# Revit family: AVAB_Roof_Exhauster
name_source: partatom
category: Mechanical Equipment
units: mm (PartAtom-declared; Revit-internal decimal feet)

## family parameters
Always vertical = Yes
Cut with Voids When Loaded = No
Part Type = Normal
Room Calculation Point = No
Round Connector Dimension = Use Diameter
Shared = No
Work Plane-Based = No

## types (8) — shared parameters
0 = 0' - 0"
1" = 0' - 1"
1.5 = 0' - 1 1/2"
2" = 0' - 2"
2' = 2' - 0"
3" = 0' - 3"
30 = 30.00°
4" = 0' - 4"
60 = 60.00°
Manufacturer = Loren Cook Company
Model = AVAB
ONE EIGTH = 0' - 0 1/8"
Type Comments = Adjustable Pitch Vane Axial Roof Exhauster Belt Drive Arrangement 9
URL = www.lorencook.com

## per-type parameters (varying)
- 35_AVAB_ROOF_EXHAUSTER: (A+.25")/2=1' - 5 7/8"; (B/2)+2"=1' - 9 15/16"; (E-.25")/2=1' - 9 3/8"; (E/2)-2"=1' - 7 1/2"; (H-(A/2))/2=1' - 3 1/16"; (T_SQ/2)+.125"=1' - 11 1/8"; -(E-.25")/2=-1' - 9 3/8"; -(E/2)+2"=-1' - 7 1/2"; -E/2=-1' - 9 1/2"; A=2' - 11 1/2"; A/2=1' - 5 3/4"; A/3=1' - 2 3/16"; B=3' - 3 7/8"; B/2=1' - 7 15/16"; C=3' - 2"; C/2=1' - 7"; C/2+L=3' - 6"; E=3' - 7"; E-2"=3' - 5"; E/2=1' - 9 1/2"; F=0' - 0 9/16"; F/2=0' - 0 9/32"; G=12' - 0"; H=3' - 11 7/8"; H+L=5' - 10 7/8"; H-(A/2)=2' - 6 1/8"; J=3' - 3 3/4"; J/2=1' - 7 7/8"; K=0' - 1 5/8"; K+K=0' - 3 1/4"; L=1' - 11"; L-(C/2)=0' - 4"; L-.125"=1' - 10 7/8"; M=3' - 5"; M/2=1' - 8 1/2"; N=1' - 0"; P=0' - 0 5/8"; P/2=0' - 0 5/16"; RO=3' - 5 1/2"; RO/2=1' - 8 3/4"; T_SQ=3' - 10"; UP_A=6' - 0"
- 39_AVAB_ROOF_EXHAUSTER: (A+.25")/2=1' - 7 13/16"; (B/2)+2"=1' - 11 31/32"; (E-.25")/2=1' - 9 3/8"; (E/2)-2"=1' - 7 1/2"; (H-(A/2))/2=1' - 3 3/32"; (T_SQ/2)+.125"=2' - 1 1/8"; -(E-.25")/2=-1' - 9 3/8"; -(E/2)+2"=-1' - 7 1/2"; -E/2=-1' - 9 1/2"; A=3' - 3 3/8"; A/2=1' - 7 11/16"; A/3=1' - 3 3/4"; B=3' - 7 15/16"; B/2=1' - 9 31/32"; C=3' - 5 7/8"; C/2=1' - 8 15/16"; C/2+L=3' - 10 15/16"; E=3' - 7"; E-2"=3' - 5"; E/2=1' - 9 1/2"; F=0' - 0 9/16"; F/2=0' - 0 9/32"; G=12' - 0"; H=4' - 1 7/8"; H+L=6' - 3 7/8"; H-(A/2)=2' - 6 3/16"; J=3' - 3 1/2"; J/2=1' - 7 3/4"; K=0' - 1 3/4"; K+K=0' - 3 1/2"; L=2' - 2"; L-(C/2)=0' - 5 1/16"; L-.125"=2' - 1 7/8"; M=3' - 9"; M/2=1' - 10 1/2"; N=1' - 1 3/8"; P=0' - 0 5/8"; P/2=0' - 0 5/16"; RO=3' - 9 1/2"; RO/2=1' - 10 3/4"; T_SQ=4' - 2"; UP_A=6' - 0"
- 44_AVAB_ROOF_EXHAUSTER: (A+.25")/2=1' - 10 3/16"; (B/2)+2"=2' - 2 13/16"; (E-.25")/2=1' - 11 3/8"; (E/2)-2"=1' - 9 1/2"; (H-(A/2))/2=1' - 3 19/32"; (T_SQ/2)+.125"=2' - 3 7/8"; -(E-.25")/2=-1' - 11 3/8"; -(E/2)+2"=-1' - 9 1/2"; -E/2=-1' - 11 1/2"; A=3' - 8 1/8"; A/2=1' - 10 1/16"; A/3=1' - 5 21/32"; B=4' - 1 5/8"; B/2=2' - 0 13/16"; C=3' - 11 3/8"; C/2=1' - 11 11/16"; C/2+L=4' - 4 3/16"; E=3' - 11"; E-2"=3' - 9"; E/2=1' - 11 1/2"; F=0' - 0 9/16"; F/2=0' - 0 9/32"; G=12' - 0"; H=4' - 5 1/4"; H+L=6' - 9 3/4"; H-(A/2)=2' - 7 3/16"; J=3' - 7 1/2"; J/2=1' - 9 3/4"; K=0' - 1 3/4"; K+K=0' - 3 1/2"; L=2' - 4 1/2"; L-(C/2)=0' - 4 13/16"; L-.125"=2' - 4 3/8"; M=4' - 3"; M/2=2' - 1 1/2"; N=1' - 3 3/8"; P=0' - 0 5/8"; P/2=0' - 0 5/16"; RO=4' - 3"; RO/2=2' - 1 1/2"; T_SQ=4' - 7 1/2"; UP_A=6' - 4"
- 49_AVAB_ROOF_EXHAUSTER: (A+.25")/2=2' - 0 3/4"; (B/2)+2"=2' - 5 3/8"; (E-.25")/2=1' - 11 3/8"; (E/2)-2"=1' - 9 1/2"; (H-(A/2))/2=1' - 2 9/16"; (T_SQ/2)+.125"=2' - 6 3/8"; -(E-.25")/2=-1' - 11 3/8"; -(E/2)+2"=-1' - 9 1/2"; -E/2=-1' - 11 1/2"; A=4' - 1 1/4"; A/2=2' - 0 5/8"; A/3=1' - 7 11/16"; B=4' - 6 3/4"; B/2=2' - 3 3/8"; C=4' - 4 1/2"; C/2=2' - 2 1/4"; C/2+L=4' - 9 3/4"; E=3' - 11"; E-2"=3' - 9"; E/2=1' - 11 1/2"; F=0' - 0 9/16"; F/2=0' - 0 9/32"; G=12' - 0"; H=4' - 5 3/4"; H+L=7' - 1 1/4"; H-(A/2)=2' - 5 1/8"; J=3' - 7 1/2"; J/2=1' - 9 3/4"; K=0' - 1 3/4"; K+K=0' - 3 1/2"; L=2' - 7 1/2"; L-(C/2)=0' - 5 1/4"; L-.125"=2' - 7 3/8"; M=4' - 8"; M/2=2' - 4"; N=1' - 5"; P=0' - 0 5/8"; P/2=0' - 0 5/16"; RO=4' - 8"; RO/2=2' - 4"; T_SQ=5' - 0 1/2"; UP_A=7' - 4 1/2"
- 57_AVAB_ROOF_EXHAUSTER: (A+.25")/2=2' - 4 11/16"; (B/2)+2"=2' - 9 5/16"; (E-.25")/2=2' - 6 3/8"; (E/2)-2"=2' - 4 1/2"; (H-(A/2))/2=1' - 6 19/32"; (T_SQ/2)+.125"=2' - 10 3/8"; -(E-.25")/2=-2' - 6 3/8"; -(E/2)+2"=-2' - 4 1/2"; -E/2=-2' - 6 1/2"; A=4' - 9 1/8"; A/2=2' - 4 9/16"; A/3=1' - 10 27/32"; B=5' - 2 5/8"; B/2=2' - 7 5/16"; C=4' - 11 7/8"; C/2=2' - 5 15/16"; C/2+L=5' - 2 15/16"; E=5' - 1"; E-2"=4' - 11"; E/2=2' - 6 1/2"; F=0' - 0 9/16"; F/2=0' - 0 9/32"; G=12' - 0"; H=5' - 5 3/4"; H+L=8' - 2 3/4"; H-(A/2)=3' - 1 3/16"; J=4' - 9 1/2"; J/2=2' - 4 3/4"; K=0' - 1 3/4"; K+K=0' - 3 1/2"; L=2' - 9"; L-(C/2)=0' - 3 1/16"; L-.125"=2' - 8 7/8"; M=5' - 8"; M/2=2' - 10"; N=1' - 9"; P=0' - 0 5/8"; P/2=0' - 0 5/16"; RO=5' - 4"; RO/2=2' - 8"; T_SQ=5' - 8 1/2"; UP_A=8' - 6 1/2"
- 63_AVAB_ROOF_EXHAUSTER: (A+.25")/2=2' - 7 5/8"; (B/2)+2"=3' - 0 1/4"; (E-.25")/2=2' - 6 3/8"; (E/2)-2"=2' - 4 1/2"; (H-(A/2))/2=1' - 6 9/16"; (T_SQ/2)+.125"=3' - 1 1/4"; -(E-.25")/2=-2' - 6 3/8"; -(E/2)+2"=-2' - 4 1/2"; -E/2=-2' - 6 1/2"; A=5' - 3"; A/2=2' - 7 1/2"; A/3=2' - 1 3/16"; B=5' - 8 1/2"; B/2=2' - 10 1/4"; C=5' - 6 1/4"; C/2=2' - 9 1/8"; C/2+L=6' - 1 1/8"; E=5' - 1"; E-2"=4' - 11"; E/2=2' - 6 1/2"; F=0' - 0 11/16"; F/2=0' - 0 11/32"; G=16' - 0"; H=5' - 8 5/8"; H+L=9' - 0 5/8"; H-(A/2)=3' - 1 1/8"; J=4' - 9 1/2"; J/2=2' - 4 3/4"; K=0' - 1 3/4"; K+K=0' - 3 1/2"; L=3' - 4"; L-(C/2)=0' - 6 7/8"; L-.125"=3' - 3 7/8"; M=5' - 10"; M/2=2' - 11"; N=1' - 9 5/8"; P=0' - 0 3/4"; P/2=0' - 0 3/8"; RO=5' - 9 3/4"; RO/2=2' - 10 7/8"; T_SQ=6' - 2 1/4"; UP_A=8' - 6 1/2"
- 71_AVAB_ROOF_EXHAUSTER: (A+.25")/2=2' - 11 9/16"; (B/2)+2"=3' - 4 13/16"; (E-.25")/2=2' - 11 7/8"; (E/2)-2"=2' - 10"; (H-(A/2))/2=1' - 6 21/32"; (T_SQ/2)+.125"=3' - 5 5/8"; -(E-.25")/2=-2' - 11 7/8"; -(E/2)+2"=-2' - 10"; -E/2=-3' - 0"; A=5' - 10 7/8"; A/2=2' - 11 7/16"; A/3=2' - 4 11/32"; B=6' - 5 5/8"; B/2=3' - 2 13/16"; C=6' - 3"; C/2=3' - 1 1/2"; C/2+L=6' - 9 1/2"; E=6' - 0"; E-2"=5' - 10"; E/2=3' - 0"; F=0' - 0 11/16"; F/2=0' - 0 11/32"; G=16' - 0"; H=6' - 0 3/4"; H+L=9' - 8 3/4"; H-(A/2)=3' - 1 5/16"; J=5' - 7 1/2"; J/2=2' - 9 3/4"; K=0' - 2 1/4"; K+K=0' - 4 1/2"; L=3' - 8"; L-(C/2)=0' - 6 1/2"; L-.125"=3' - 7 7/8"; M=6' - 6 1/2"; M/2=3' - 3 1/4"; N=2' - 0 3/8"; P=0' - 0 3/4"; P/2=0' - 0 3/8"; RO=6' - 6 1/2"; RO/2=3' - 3 1/4"; T_SQ=6' - 11"; UP_A=9' - 5 1/2"
- 79_AVAB_ROOF_EXHAUSTER: (A+.25")/2=3' - 3 1/2"; (B/2)+2"=3' - 8 25/32"; (E-.25")/2=2' - 11 7/8"; (E/2)-2"=2' - 10"; (H-(A/2))/2=1' - 6 5/8"; (T_SQ/2)+.125"=3' - 9 5/8"; -(E-.25")/2=-2' - 11 7/8"; -(E/2)+2"=-2' - 10"; -E/2=-3' - 0"; A=6' - 6 3/4"; A/2=3' - 3 3/8"; A/3=2' - 7 1/2"; B=7' - 1 9/16"; B/2=3' - 6 25/32"; C=6' - 10 7/8"; C/2=3' - 5 7/16"; C/2+L=7' - 4 15/16"; E=6' - 0"; E-2"=5' - 10"; E/2=3' - 0"; F=0' - 0 11/16"; F/2=0' - 0 11/32"; G=16' - 0"; H=6' - 4 5/8"; H+L=10' - 4 1/8"; H-(A/2)=3' - 1 1/4"; J=5' - 7 1/2"; J/2=2' - 9 3/4"; K=0' - 2 1/4"; K+K=0' - 4 1/2"; L=3' - 11 1/2"; L-(C/2)=0' - 6 1/16"; L-.125"=3' - 11 3/8"; M=7' - 3"; M/2=3' - 7 1/2"; N=2' - 3 3/8"; P=0' - 0 3/4"; P/2=0' - 0 3/8"; RO=7' - 2 1/2"; RO/2=3' - 7 1/4"; T_SQ=7' - 7"; UP_A=9' - 9 5/8"

## geometry (parser evidence)
native form markers: Sweep x2
no freeform markers — native parametric forms only
